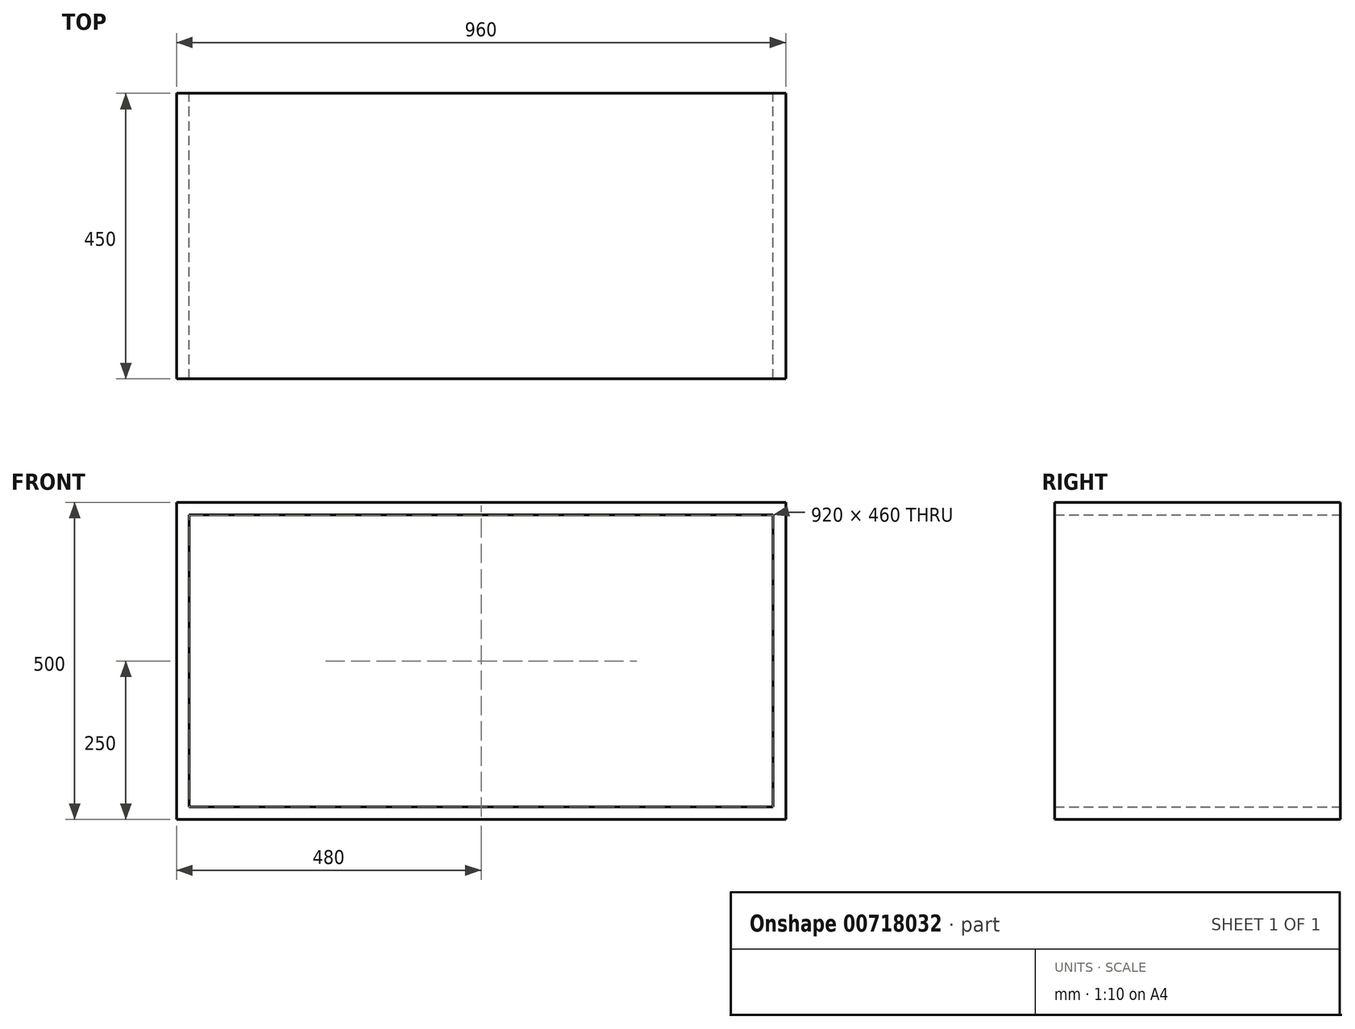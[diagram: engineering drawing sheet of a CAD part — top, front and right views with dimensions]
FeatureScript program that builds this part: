
annotation { "Feature Type Name" : "Feature", "Feature Type Description" : "" }
export const myFeature = defineFeature(function(context is Context, id is Id, definition is map)
    precondition{}
    {
        {
            var Q0;
            Q0=qCreatedBy(makeId("Front.planeOp"),FACE);
            var sketch = newSketch(context, id + "F0", { "sketchPlane" : qUnion([Q0])});
            skLineSegment(sketch, "E0.bottom", {"start": v(480, 250) * mm, "end": v(-480, 250) * mm});
            skLineSegment(sketch, "E0.top", {"start": v(480, -250) * mm, "end": v(-480, -250) * mm});
            skLineSegment(sketch, "E0.left", {"start": v(480, 250) * mm, "end": v(480, -250) * mm});
            skLineSegment(sketch, "E0.right", {"start": v(-480, 250) * mm, "end": v(-480, -250) * mm});
            skPoint(sketch, "E0.middle", {"position": v(0, 0) * mm});
            skLineSegment(sketch, "E1.0", {"start": v(-460, 230) * mm, "end": v(-460, -230) * mm});
            skLineSegment(sketch, "E1.1", {"start": v(460, 230) * mm, "end": v(-460, 230) * mm});
            skLineSegment(sketch, "E1.2", {"start": v(460, 230) * mm, "end": v(460, -230) * mm});
            skLineSegment(sketch, "E1.3", {"start": v(460, -230) * mm, "end": v(-460, -230) * mm});
            skSolve(sketch);
        }
        {
            var Q0;
            Q0=qSketchRegion(id+"F0",true);
            extrude(context, id + "F1", {"entities" : qUnion([Q0]), "depth" : 450 * mm, "offsetDistance" : 25 * mm});
        }
    });
